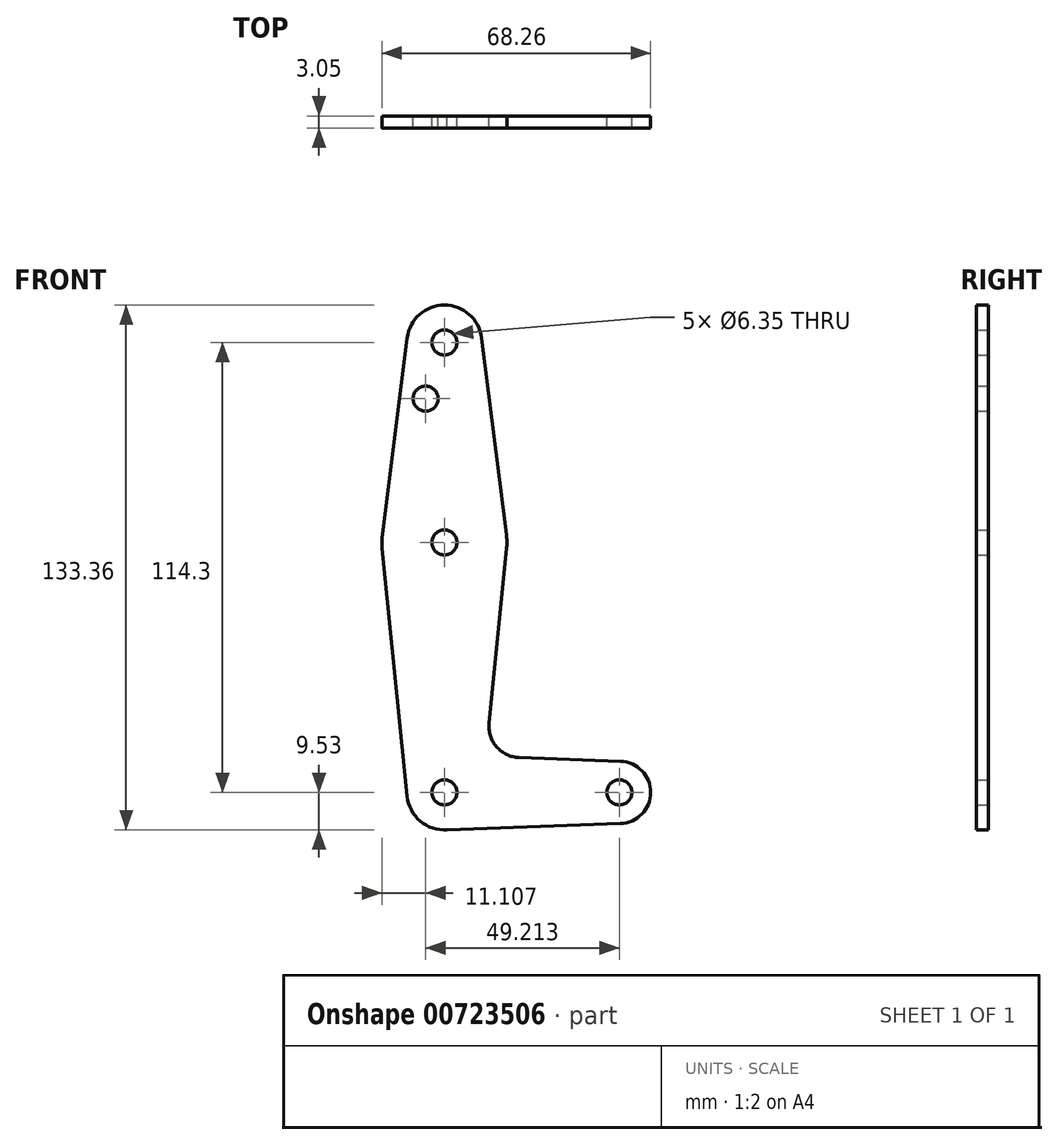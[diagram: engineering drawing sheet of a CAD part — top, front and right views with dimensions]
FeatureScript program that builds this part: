
annotation { "Feature Type Name" : "Feature", "Feature Type Description" : "" }
export const myFeature = defineFeature(function(context is Context, id is Id, definition is map)
    precondition{}
    {
        {
            var Q0;
            Q0=qCreatedBy(makeId("Front.planeOp"),FACE);
            var sketch = newSketch(context, id + "F0", { "sketchPlane" : qUnion([Q0])});
            skLineSegment(sketch, "E0", {"start": v(0, 0) * mm, "end": v(0, 114.3) * mm, "construction": true});
            skLineSegment(sketch, "E1", {"start": v(0, 0) * mm, "end": v(44.45, 0) * mm, "construction": true});
            skCircle(sketch, "E2", {"center": v(0, 114.3) * mm, "radius": 9.53 * mm});
            skCircle(sketch, "E3", {"center": v(0, 63.5) * mm, "radius": 15.88 * mm});
            skCircle(sketch, "E4", {"center": v(0, 0) * mm, "radius": 9.53 * mm});
            skCircle(sketch, "E5", {"center": v(44.45, 0) * mm, "radius": 7.94 * mm});
            skLineSegment(sketch, "E6", {"start": v(9.45, 115.5) * mm, "end": v(15.75, 65.48) * mm});
            skLineSegment(sketch, "E7", {"start": v(-9.45, 115.5) * mm, "end": v(-15.75, 65.48) * mm});
            skLineSegment(sketch, "E8", {"start": v(0, -9.53) * mm, "end": v(44.73, -7.93) * mm});
            skCircle(sketch, "E9", {"center": v(0, 114.3) * mm, "radius": 3.18 * mm});
            skCircle(sketch, "E10", {"center": v(0, 63.5) * mm, "radius": 3.18 * mm});
            skCircle(sketch, "E11", {"center": v(0, 0) * mm, "radius": 3.18 * mm});
            skCircle(sketch, "E12", {"center": v(44.45, 0) * mm, "radius": 3.18 * mm});
            skPoint(sketch, "E13.newPointB", {"position": v(0, 9.53) * mm});
            skLineSegment(sketch, "E14", {"start": v(44.73, 7.93) * mm, "end": v(18.97, 8.85) * mm});
            skLineSegment(sketch, "E15", {"start": v(-9.48, -0.95) * mm, "end": v(-15.8, 61.91) * mm});
            skLineSegment(sketch, "E16", {"start": v(11.34, 17.6) * mm, "end": v(15.8, 61.91) * mm});
            skCircle(sketch, "E17", {"center": v(-4.76, 100.03) * mm, "radius": 3.18 * mm});
            skArc(sketch, "E18.filletArc", {"start": v(11.34, 17.6) * mm, "mid": v(13.26, 11.57) * mm, "end": v(18.97, 8.85) * mm});
            skSolve(sketch);
        }
        {
            var Q0;
            Q0 = qSketchRegion(id + "F0", true);
            extrude(context, id + "F1", {"entities" : qUnion([Q0]), "depth" : 3.05 * mm, "offsetDistance" : 25.4 * mm});
        }
    });
